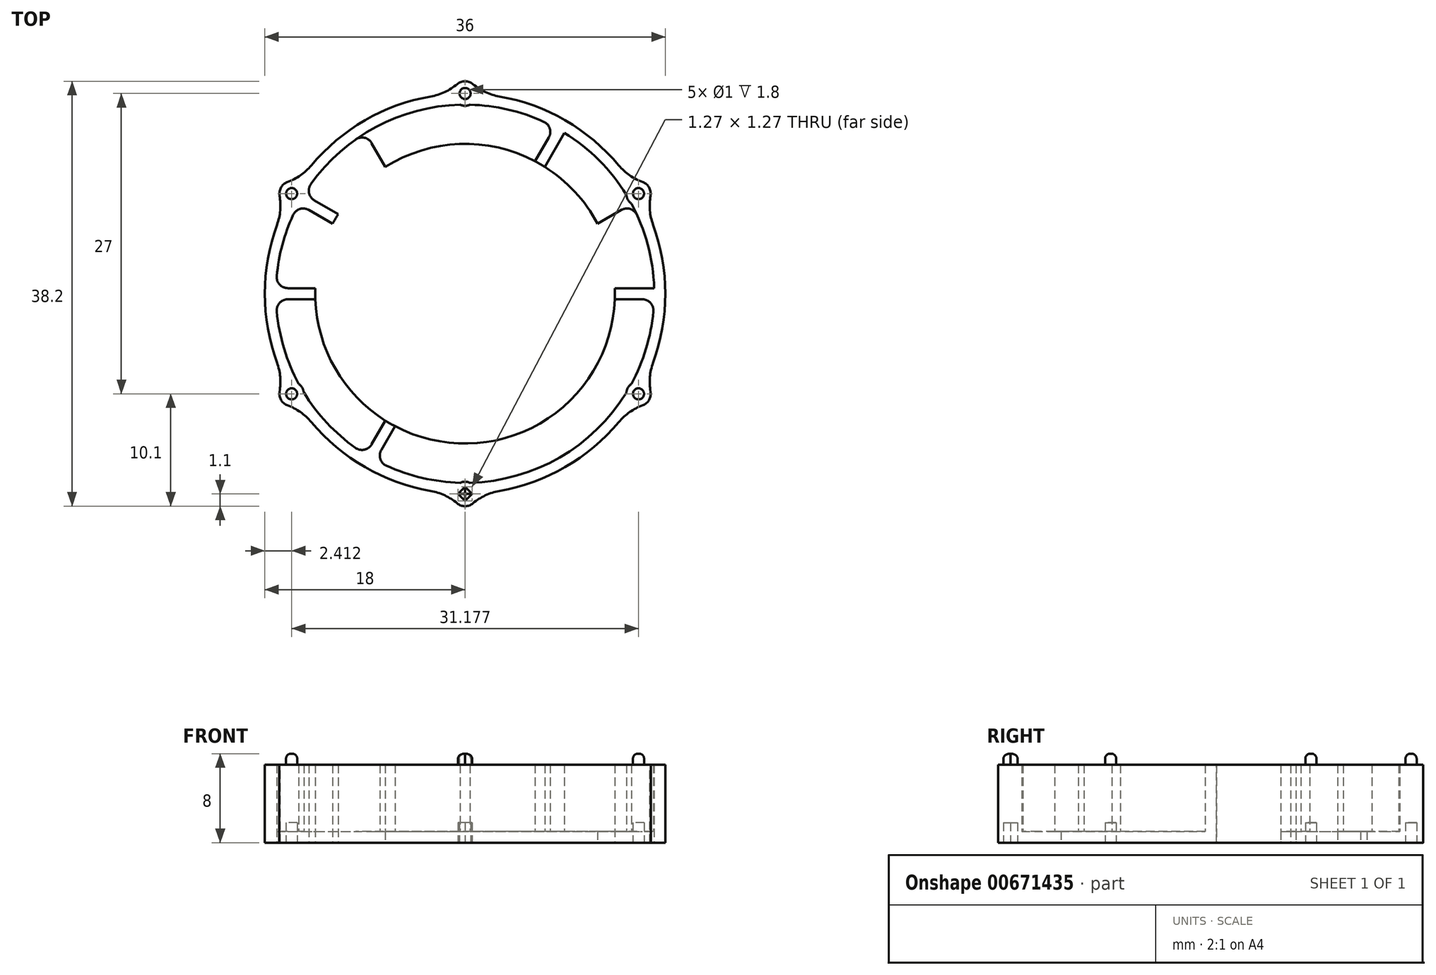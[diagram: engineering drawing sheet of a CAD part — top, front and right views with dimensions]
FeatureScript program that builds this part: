
annotation { "Feature Type Name" : "Feature", "Feature Type Description" : "" }
export const myFeature = defineFeature(function(context is Context, id is Id, definition is map)
    precondition{}
    {
        {
            var Q0;
            Q0=qCreatedBy(makeId("Top.planeOp"),FACE);
            var sketch = newSketch(context, id + "F0", { "sketchPlane" : qUnion([Q0])});
            skCircle(sketch, "E0", {"center": v(0, 0) * mm, "radius": 18 * mm});
            skCircle(sketch, "E1.0", {"center": v(0, 0) * mm, "radius": 17 * mm});
            skLineSegment(sketch, "E2.bottom", {"start": v(8.56, 15.83) * mm, "end": v(9.43, 15.33) * mm});
            skLineSegment(sketch, "E2.top", {"start": v(-9.43, -15.33) * mm, "end": v(-8.56, -15.83) * mm});
            skLineSegment(sketch, "E2.left", {"start": v(8.56, 15.83) * mm, "end": v(-9.43, -15.33) * mm});
            skLineSegment(sketch, "E2.right", {"start": v(9.43, 15.33) * mm, "end": v(-8.56, -15.83) * mm});
            skLineSegment(sketch, "E3.bottom", {"start": v(15.33, 9.43) * mm, "end": v(15.83, 8.56) * mm});
            skLineSegment(sketch, "E3.top", {"start": v(-15.83, -8.56) * mm, "end": v(-15.33, -9.43) * mm});
            skLineSegment(sketch, "E3.left", {"start": v(15.33, 9.43) * mm, "end": v(-15.83, -8.56) * mm});
            skLineSegment(sketch, "E3.right", {"start": v(15.83, 8.56) * mm, "end": v(-15.33, -9.43) * mm});
            skLineSegment(sketch, "E4", {"start": v(-38.35, 0) * mm, "end": v(39.17, 0) * mm, "construction": true});
            skLineSegment(sketch, "E5", {"start": v(0, 42.5) * mm, "end": v(0, -42.47) * mm, "construction": true});
            skLineSegment(sketch, "E6.bottom", {"start": v(-18, 0.5) * mm, "end": v(18, 0.5) * mm});
            skLineSegment(sketch, "E6.top", {"start": v(-18, -0.5) * mm, "end": v(18, -0.5) * mm});
            skLineSegment(sketch, "E6.left", {"start": v(-18, 0.5) * mm, "end": v(-18, -0.5) * mm});
            skLineSegment(sketch, "E6.right", {"start": v(18, 0.5) * mm, "end": v(18, -0.5) * mm});
            skLineSegment(sketch, "E7.bottom", {"start": v(-15.33, 9.43) * mm, "end": v(15.83, -8.56) * mm});
            skLineSegment(sketch, "E7.top", {"start": v(-15.83, 8.56) * mm, "end": v(15.33, -9.43) * mm});
            skLineSegment(sketch, "E7.left", {"start": v(-15.33, 9.43) * mm, "end": v(-15.83, 8.56) * mm});
            skLineSegment(sketch, "E7.right", {"start": v(15.83, -8.56) * mm, "end": v(15.33, -9.43) * mm});
            skLineSegment(sketch, "E8.bottom", {"start": v(-0.5, 18) * mm, "end": v(0.5, 18) * mm});
            skLineSegment(sketch, "E8.top", {"start": v(-0.5, -18) * mm, "end": v(0.5, -18) * mm});
            skLineSegment(sketch, "E8.left", {"start": v(-0.5, 18) * mm, "end": v(-0.5, -18) * mm});
            skLineSegment(sketch, "E8.right", {"start": v(0.5, 18) * mm, "end": v(0.5, -18) * mm});
            skLineSegment(sketch, "E9.bottom", {"start": v(-9.43, 15.33) * mm, "end": v(-8.56, 15.83) * mm});
            skLineSegment(sketch, "E9.top", {"start": v(8.56, -15.83) * mm, "end": v(9.43, -15.33) * mm});
            skLineSegment(sketch, "E9.left", {"start": v(-9.43, 15.33) * mm, "end": v(8.56, -15.83) * mm});
            skLineSegment(sketch, "E9.right", {"start": v(-8.56, 15.83) * mm, "end": v(9.43, -15.33) * mm});
            skCircle(sketch, "E10", {"center": v(0, 0) * mm, "radius": 13.47 * mm});
            skSolve(sketch);
        }
        {
            var Q0;
            Q0=qCreatedBy(makeId("Top.planeOp"),FACE);
            var sketch = newSketch(context, id + "F1", { "sketchPlane" : qUnion([Q0])});
            skCircle(sketch, "E11", {"center": v(0, 0) * mm, "radius": 18 * mm});
            skCircle(sketch, "E12", {"center": v(0, 0) * mm, "radius": 17 * mm});
            skSolve(sketch);
        }
        {
            var Q0;
            Q0=makeQuery(id+"F1.imprint","IMPRINT",FACE,{"disambiguationData":[TD([[makeQuery(id+"F1.imprint","IMPRINT",EDGE,{"derivedFrom":sQuery(id+"F1.wireOp",EDGE,"E11")}),1.0]])]});
            extrude(context, id + "F2", {"entities" : qUnion([Q0]), "depth" : 7 * mm, "offsetDistance" : 25 * mm});
        }
        {
            var Q0;
            {var subQ0=sQuery(id+"F0.wireOp",EDGE,"E7.bottom");var subQ1=sQuery(id+"F0.wireOp",EDGE,"E1.0");var subQ2=makeQuery(id+"F0.imprint","INTERSECT",VERTEX,{"disambiguationData":[OD(0.0)],"derivedFrom":[subQ1,subQ0]});Q0=makeQuery(id+"F0.imprint","IMPRINT",FACE,{"disambiguationData":[TD([[makeQuery(id+"F0.imprint","IMPRINT",EDGE,{"disambiguationData":[TD([[subQ2,-1.0]])],"derivedFrom":subQ1}),1.0]])]});}
            var Q1;
            {var subQ0=sQuery(id+"F0.wireOp",EDGE,"E2.right");var subQ1=sQuery(id+"F0.wireOp",EDGE,"E1.0");var subQ2=makeQuery(id+"F0.imprint","INTERSECT",VERTEX,{"disambiguationData":[OD(0.0)],"derivedFrom":[subQ1,subQ0]});Q1=makeQuery(id+"F0.imprint","IMPRINT",FACE,{"disambiguationData":[TD([[makeQuery(id+"F0.imprint","IMPRINT",EDGE,{"disambiguationData":[TD([[subQ2,-1.0]])],"derivedFrom":subQ1}),1.0]])]});}
            var Q2;
            {var subQ0=sQuery(id+"F0.wireOp",EDGE,"E6.bottom");var subQ1=sQuery(id+"F0.wireOp",EDGE,"E1.0");var subQ2=makeQuery(id+"F0.imprint","INTERSECT",VERTEX,{"disambiguationData":[OD(0.0)],"derivedFrom":[subQ1,subQ0]});Q2=makeQuery(id+"F0.imprint","IMPRINT",FACE,{"disambiguationData":[TD([[makeQuery(id+"F0.imprint","IMPRINT",EDGE,{"disambiguationData":[TD([[subQ2,1.0]])],"derivedFrom":subQ1}),1.0]])]});}
            var Q3;
            {var subQ0=sQuery(id+"F0.wireOp",EDGE,"E2.left");var subQ1=sQuery(id+"F0.wireOp",EDGE,"E1.0");var subQ2=makeQuery(id+"F0.imprint","INTERSECT",VERTEX,{"disambiguationData":[OD(1.0)],"derivedFrom":[subQ1,subQ0]});Q3=makeQuery(id+"F0.imprint","IMPRINT",FACE,{"disambiguationData":[TD([[makeQuery(id+"F0.imprint","IMPRINT",EDGE,{"disambiguationData":[TD([[subQ2,-1.0]])],"derivedFrom":subQ1}),1.0]])]});}
            var Q4;
            {var subQ0=sQuery(id+"F0.wireOp",EDGE,"E6.bottom");var subQ1=sQuery(id+"F0.wireOp",EDGE,"E1.0");var subQ2=makeQuery(id+"F0.imprint","INTERSECT",VERTEX,{"disambiguationData":[OD(1.0)],"derivedFrom":[subQ1,subQ0]});Q4=makeQuery(id+"F0.imprint","IMPRINT",FACE,{"disambiguationData":[TD([[makeQuery(id+"F0.imprint","IMPRINT",EDGE,{"disambiguationData":[TD([[subQ2,-1.0]])],"derivedFrom":subQ1}),1.0]])]});}
            extrude(context, id + "F3", {"entities" : qUnion([Q0, Q1, Q2, Q3, Q4]), "operationType" : NewBodyOperationType.ADD, "depth" : 7 * mm, "offsetDistance" : 25 * mm});
        }
        {
            var Q0;
            Q0=makeQuery(id+"F1.imprint","IMPRINT",FACE,{"disambiguationData":[TD([[makeQuery(id+"F1.imprint","IMPRINT",EDGE,{"derivedFrom":sQuery(id+"F1.wireOp",EDGE,"E11")}),1.0]])]});
            var Q1;
            Q1=makeQuery(id+"F1.imprint","IMPRINT",FACE,{"disambiguationData":[TD([[makeQuery(id+"F1.imprint","IMPRINT",EDGE,{"derivedFrom":sQuery(id+"F1.wireOp",EDGE,"E12")}),1.0]])]});
            extrude(context, id + "F4", {"entities" : qUnion([Q0, Q1]), "operationType" : NewBodyOperationType.ADD, "depth" : 1 * mm, "offsetDistance" : 25 * mm});
        }
        {
            var Q0;
            Q0=qCreatedBy(makeId("Top.planeOp"),FACE);
            var sketch = newSketch(context, id + "F5", { "sketchPlane" : qUnion([Q0])});
            skCircle(sketch, "E13", {"center": v(0, 0) * mm, "radius": 18 * mm});
            skLineSegment(sketch, "E14", {"start": v(0, 18) * mm, "end": v(0, -18) * mm, "construction": true});
            skLineSegment(sketch, "E15", {"start": v(15.59, 9) * mm, "end": v(0, 0) * mm, "construction": true});
            skLineSegment(sketch, "E16", {"start": v(9, 15.59) * mm, "end": v(0, 0) * mm, "construction": true});
            skLineSegment(sketch, "E17", {"start": v(0, 0) * mm, "end": v(18, 0) * mm, "construction": true});
            skLineSegment(sketch, "E18", {"start": v(0, 0) * mm, "end": v(15.59, -9) * mm, "construction": true});
            skLineSegment(sketch, "E19", {"start": v(0, 0) * mm, "end": v(9, -15.59) * mm, "construction": true});
            skLineSegment(sketch, "E20", {"start": v(0, 0) * mm, "end": v(-9, 15.59) * mm, "construction": true});
            skLineSegment(sketch, "E21", {"start": v(0, 0) * mm, "end": v(-15.59, 9) * mm, "construction": true});
            skLineSegment(sketch, "E22", {"start": v(0, 0) * mm, "end": v(-18, 0) * mm, "construction": true});
            skLineSegment(sketch, "E23", {"start": v(0, 0) * mm, "end": v(-15.59, -9) * mm, "construction": true});
            skLineSegment(sketch, "E24", {"start": v(0, 0) * mm, "end": v(-9, -15.59) * mm, "construction": true});
            skCircle(sketch, "E25", {"center": v(0, 18) * mm, "radius": 1.1 * mm});
            skCircle(sketch, "E26", {"center": v(15.59, 9) * mm, "radius": 1.1 * mm});
            skCircle(sketch, "E27", {"center": v(15.59, -9) * mm, "radius": 1.1 * mm});
            skCircle(sketch, "E28", {"center": v(0, -18) * mm, "radius": 1.1 * mm});
            skCircle(sketch, "E29", {"center": v(-15.59, -9) * mm, "radius": 1.1 * mm});
            skCircle(sketch, "E30", {"center": v(-15.59, 9) * mm, "radius": 1.1 * mm});
            skCircle(sketch, "E31", {"center": v(-15.59, 9) * mm, "radius": 0.5 * mm});
            skCircle(sketch, "E32", {"center": v(0, 18) * mm, "radius": 0.5 * mm});
            skCircle(sketch, "E33", {"center": v(15.59, 9) * mm, "radius": 0.5 * mm});
            skCircle(sketch, "E34", {"center": v(15.59, -9) * mm, "radius": 0.5 * mm});
            skCircle(sketch, "E35", {"center": v(-15.59, -9) * mm, "radius": 0.5 * mm});
            skLineSegment(sketch, "E36.bottom", {"start": v(0.64, -18) * mm, "end": v(0, -18.64) * mm});
            skLineSegment(sketch, "E36.top", {"start": v(0, -17.36) * mm, "end": v(-0.64, -18) * mm});
            skLineSegment(sketch, "E36.left", {"start": v(0.64, -18) * mm, "end": v(0, -17.36) * mm});
            skLineSegment(sketch, "E36.right", {"start": v(0, -18.64) * mm, "end": v(-0.64, -18) * mm});
            skSolve(sketch);
        }
        {
            var Q0;
            {var subQ0=sQuery(id+"F5.wireOp",EDGE,"E30");var subQ1=sQuery(id+"F5.wireOp",EDGE,"E13");var subQ2=makeQuery(id+"F5.imprint","INTERSECT",VERTEX,{"disambiguationData":[OD(0.0)],"derivedFrom":[subQ1,subQ0]});Q0=makeQuery(id+"F5.imprint","IMPRINT",FACE,{"disambiguationData":[TD([[makeQuery(id+"F5.imprint","IMPRINT",EDGE,{"disambiguationData":[TD([[subQ2,-1.0]])],"derivedFrom":subQ1}),1.0]])]});}
            var Q1;
            {var subQ0=sQuery(id+"F5.wireOp",EDGE,"E30");var subQ1=sQuery(id+"F5.wireOp",EDGE,"E13");var subQ2=makeQuery(id+"F5.imprint","INTERSECT",VERTEX,{"disambiguationData":[OD(0.0)],"derivedFrom":[subQ1,subQ0]});Q1=makeQuery(id+"F5.imprint","IMPRINT",FACE,{"disambiguationData":[TD([[makeQuery(id+"F5.imprint","IMPRINT",EDGE,{"disambiguationData":[TD([[subQ2,-1.0]])],"derivedFrom":subQ1}),-1.0]])]});}
            var Q2;
            {var subQ0=sQuery(id+"F5.wireOp",EDGE,"E25");var subQ1=sQuery(id+"F5.wireOp",EDGE,"E13");var subQ2=makeQuery(id+"F5.imprint","INTERSECT",VERTEX,{"disambiguationData":[OD(0.0)],"derivedFrom":[subQ1,subQ0]});Q2=makeQuery(id+"F5.imprint","IMPRINT",FACE,{"disambiguationData":[TD([[makeQuery(id+"F5.imprint","IMPRINT",EDGE,{"disambiguationData":[TD([[subQ2,-1.0]])],"derivedFrom":subQ1}),1.0]])]});}
            var Q3;
            {var subQ0=sQuery(id+"F5.wireOp",EDGE,"E25");var subQ1=sQuery(id+"F5.wireOp",EDGE,"E13");var subQ2=makeQuery(id+"F5.imprint","INTERSECT",VERTEX,{"disambiguationData":[OD(0.0)],"derivedFrom":[subQ1,subQ0]});Q3=makeQuery(id+"F5.imprint","IMPRINT",FACE,{"disambiguationData":[TD([[makeQuery(id+"F5.imprint","IMPRINT",EDGE,{"disambiguationData":[TD([[subQ2,-1.0]])],"derivedFrom":subQ1}),-1.0]])]});}
            var Q4;
            {var subQ0=sQuery(id+"F5.wireOp",EDGE,"E26");var subQ1=sQuery(id+"F5.wireOp",EDGE,"E13");var subQ2=makeQuery(id+"F5.imprint","INTERSECT",VERTEX,{"disambiguationData":[OD(0.0)],"derivedFrom":[subQ1,subQ0]});Q4=makeQuery(id+"F5.imprint","IMPRINT",FACE,{"disambiguationData":[TD([[makeQuery(id+"F5.imprint","IMPRINT",EDGE,{"disambiguationData":[TD([[subQ2,-1.0]])],"derivedFrom":subQ1}),-1.0]])]});}
            var Q5;
            {var subQ0=sQuery(id+"F5.wireOp",EDGE,"E26");var subQ1=sQuery(id+"F5.wireOp",EDGE,"E13");var subQ2=makeQuery(id+"F5.imprint","INTERSECT",VERTEX,{"disambiguationData":[OD(0.0)],"derivedFrom":[subQ1,subQ0]});Q5=makeQuery(id+"F5.imprint","IMPRINT",FACE,{"disambiguationData":[TD([[makeQuery(id+"F5.imprint","IMPRINT",EDGE,{"disambiguationData":[TD([[subQ2,-1.0]])],"derivedFrom":subQ1}),1.0]])]});}
            var Q6;
            {var subQ0=sQuery(id+"F5.wireOp",EDGE,"E29");var subQ1=sQuery(id+"F5.wireOp",EDGE,"E13");var subQ2=makeQuery(id+"F5.imprint","INTERSECT",VERTEX,{"disambiguationData":[OD(0.0)],"derivedFrom":[subQ1,subQ0]});Q6=makeQuery(id+"F5.imprint","IMPRINT",FACE,{"disambiguationData":[TD([[makeQuery(id+"F5.imprint","IMPRINT",EDGE,{"disambiguationData":[TD([[subQ2,-1.0]])],"derivedFrom":subQ1}),1.0]])]});}
            var Q7;
            {var subQ0=sQuery(id+"F5.wireOp",EDGE,"E29");var subQ1=sQuery(id+"F5.wireOp",EDGE,"E13");var subQ2=makeQuery(id+"F5.imprint","INTERSECT",VERTEX,{"disambiguationData":[OD(0.0)],"derivedFrom":[subQ1,subQ0]});Q7=makeQuery(id+"F5.imprint","IMPRINT",FACE,{"disambiguationData":[TD([[makeQuery(id+"F5.imprint","IMPRINT",EDGE,{"disambiguationData":[TD([[subQ2,-1.0]])],"derivedFrom":subQ1}),-1.0]])]});}
            var Q8;
            {var subQ3=sQuery(id+"F5.wireOp",EDGE,"E13");var subQ5=sQuery(id+"F5.wireOp",EDGE,"E28");var subQ6=makeQuery(id+"F5.imprint","INTERSECT",VERTEX,{"disambiguationData":[OD(0.0)],"derivedFrom":[subQ3,subQ5]});Q8=makeQuery(id+"F5.imprint","IMPRINT",FACE,{"disambiguationData":[TD([[makeQuery(id+"F5.imprint","IMPRINT",EDGE,{"disambiguationData":[TD([[subQ6,-1.0]])],"derivedFrom":subQ3}),1.0]])]});}
            var Q9;
            {var subQ6=sQuery(id+"F5.wireOp",EDGE,"E36.bottom");Q9=makeQuery(id+"F5.imprint","IMPRINT",FACE,{"disambiguationData":[TD([[makeQuery(id+"F5.imprint","IMPRINT",EDGE,{"derivedFrom":subQ6}),1.0]])]});}
            var Q10;
            {var subQ0=sQuery(id+"F5.wireOp",EDGE,"E27");var subQ1=sQuery(id+"F5.wireOp",EDGE,"E13");var subQ2=makeQuery(id+"F5.imprint","INTERSECT",VERTEX,{"disambiguationData":[OD(0.0)],"derivedFrom":[subQ1,subQ0]});Q10=makeQuery(id+"F5.imprint","IMPRINT",FACE,{"disambiguationData":[TD([[makeQuery(id+"F5.imprint","IMPRINT",EDGE,{"disambiguationData":[TD([[subQ2,-1.0]])],"derivedFrom":subQ1}),-1.0]])]});}
            var Q11;
            {var subQ0=sQuery(id+"F5.wireOp",EDGE,"E27");var subQ1=sQuery(id+"F5.wireOp",EDGE,"E13");var subQ2=makeQuery(id+"F5.imprint","INTERSECT",VERTEX,{"disambiguationData":[OD(0.0)],"derivedFrom":[subQ1,subQ0]});Q11=makeQuery(id+"F5.imprint","IMPRINT",FACE,{"disambiguationData":[TD([[makeQuery(id+"F5.imprint","IMPRINT",EDGE,{"disambiguationData":[TD([[subQ2,-1.0]])],"derivedFrom":subQ1}),1.0]])]});}
            var Q12;
            {var subQ0=sQuery(id+"F5.wireOp",EDGE,"E31");var subQ1=sQuery(id+"F5.wireOp",EDGE,"E13");var subQ2=makeQuery(id+"F5.imprint","INTERSECT",VERTEX,{"disambiguationData":[OD(0.0)],"derivedFrom":[subQ1,subQ0]});Q12=makeQuery(id+"F5.imprint","IMPRINT",FACE,{"disambiguationData":[TD([[makeQuery(id+"F5.imprint","IMPRINT",EDGE,{"disambiguationData":[TD([[subQ2,-1.0]])],"derivedFrom":subQ1}),1.0]])]});}
            var Q13;
            {var subQ0=sQuery(id+"F5.wireOp",EDGE,"E31");var subQ1=sQuery(id+"F5.wireOp",EDGE,"E13");var subQ2=makeQuery(id+"F5.imprint","INTERSECT",VERTEX,{"disambiguationData":[OD(0.0)],"derivedFrom":[subQ1,subQ0]});Q13=makeQuery(id+"F5.imprint","IMPRINT",FACE,{"disambiguationData":[TD([[makeQuery(id+"F5.imprint","IMPRINT",EDGE,{"disambiguationData":[TD([[subQ2,-1.0]])],"derivedFrom":subQ1}),-1.0]])]});}
            var Q14;
            {var subQ0=sQuery(id+"F5.wireOp",EDGE,"E32");var subQ1=sQuery(id+"F5.wireOp",EDGE,"E13");var subQ2=makeQuery(id+"F5.imprint","INTERSECT",VERTEX,{"disambiguationData":[OD(0.0)],"derivedFrom":[subQ1,subQ0]});Q14=makeQuery(id+"F5.imprint","IMPRINT",FACE,{"disambiguationData":[TD([[makeQuery(id+"F5.imprint","IMPRINT",EDGE,{"disambiguationData":[TD([[subQ2,-1.0]])],"derivedFrom":subQ1}),-1.0]])]});}
            var Q15;
            {var subQ0=sQuery(id+"F5.wireOp",EDGE,"E32");var subQ1=sQuery(id+"F5.wireOp",EDGE,"E13");var subQ2=makeQuery(id+"F5.imprint","INTERSECT",VERTEX,{"disambiguationData":[OD(0.0)],"derivedFrom":[subQ1,subQ0]});Q15=makeQuery(id+"F5.imprint","IMPRINT",FACE,{"disambiguationData":[TD([[makeQuery(id+"F5.imprint","IMPRINT",EDGE,{"disambiguationData":[TD([[subQ2,-1.0]])],"derivedFrom":subQ1}),1.0]])]});}
            var Q16;
            {var subQ0=sQuery(id+"F5.wireOp",EDGE,"E33");var subQ1=sQuery(id+"F5.wireOp",EDGE,"E13");var subQ2=makeQuery(id+"F5.imprint","INTERSECT",VERTEX,{"disambiguationData":[OD(0.0)],"derivedFrom":[subQ1,subQ0]});Q16=makeQuery(id+"F5.imprint","IMPRINT",FACE,{"disambiguationData":[TD([[makeQuery(id+"F5.imprint","IMPRINT",EDGE,{"disambiguationData":[TD([[subQ2,-1.0]])],"derivedFrom":subQ1}),-1.0]])]});}
            var Q17;
            {var subQ0=sQuery(id+"F5.wireOp",EDGE,"E33");var subQ1=sQuery(id+"F5.wireOp",EDGE,"E13");var subQ2=makeQuery(id+"F5.imprint","INTERSECT",VERTEX,{"disambiguationData":[OD(0.0)],"derivedFrom":[subQ1,subQ0]});Q17=makeQuery(id+"F5.imprint","IMPRINT",FACE,{"disambiguationData":[TD([[makeQuery(id+"F5.imprint","IMPRINT",EDGE,{"disambiguationData":[TD([[subQ2,-1.0]])],"derivedFrom":subQ1}),1.0]])]});}
            var Q18;
            {var subQ0=sQuery(id+"F5.wireOp",EDGE,"E34");var subQ1=sQuery(id+"F5.wireOp",EDGE,"E13");var subQ2=makeQuery(id+"F5.imprint","INTERSECT",VERTEX,{"disambiguationData":[OD(0.0)],"derivedFrom":[subQ1,subQ0]});Q18=makeQuery(id+"F5.imprint","IMPRINT",FACE,{"disambiguationData":[TD([[makeQuery(id+"F5.imprint","IMPRINT",EDGE,{"disambiguationData":[TD([[subQ2,-1.0]])],"derivedFrom":subQ1}),-1.0]])]});}
            var Q19;
            {var subQ0=sQuery(id+"F5.wireOp",EDGE,"E34");var subQ1=sQuery(id+"F5.wireOp",EDGE,"E13");var subQ2=makeQuery(id+"F5.imprint","INTERSECT",VERTEX,{"disambiguationData":[OD(0.0)],"derivedFrom":[subQ1,subQ0]});Q19=makeQuery(id+"F5.imprint","IMPRINT",FACE,{"disambiguationData":[TD([[makeQuery(id+"F5.imprint","IMPRINT",EDGE,{"disambiguationData":[TD([[subQ2,-1.0]])],"derivedFrom":subQ1}),1.0]])]});}
            var Q20;
            {var subQ1=sQuery(id+"F5.wireOp",EDGE,"E36.bottom");Q20=makeQuery(id+"F5.imprint","IMPRINT",FACE,{"disambiguationData":[TD([[makeQuery(id+"F5.imprint","IMPRINT",EDGE,{"derivedFrom":subQ1}),-1.0]])]});}
            var Q21;
            {var subQ0=sQuery(id+"F5.wireOp",EDGE,"E35");var subQ1=sQuery(id+"F5.wireOp",EDGE,"E13");var subQ2=makeQuery(id+"F5.imprint","INTERSECT",VERTEX,{"disambiguationData":[OD(0.0)],"derivedFrom":[subQ1,subQ0]});Q21=makeQuery(id+"F5.imprint","IMPRINT",FACE,{"disambiguationData":[TD([[makeQuery(id+"F5.imprint","IMPRINT",EDGE,{"disambiguationData":[TD([[subQ2,-1.0]])],"derivedFrom":subQ1}),-1.0]])]});}
            var Q22;
            {var subQ0=sQuery(id+"F5.wireOp",EDGE,"E35");var subQ1=sQuery(id+"F5.wireOp",EDGE,"E13");var subQ2=makeQuery(id+"F5.imprint","INTERSECT",VERTEX,{"disambiguationData":[OD(0.0)],"derivedFrom":[subQ1,subQ0]});Q22=makeQuery(id+"F5.imprint","IMPRINT",FACE,{"disambiguationData":[TD([[makeQuery(id+"F5.imprint","IMPRINT",EDGE,{"disambiguationData":[TD([[subQ2,-1.0]])],"derivedFrom":subQ1}),1.0]])]});}
            var Q23;
            {var subQ0=sQuery(id+"F5.wireOp",EDGE,"E36.top");var subQ1=sQuery(id+"F5.wireOp",EDGE,"E13");var subQ2=makeQuery(id+"F5.imprint","INTERSECT",VERTEX,{"derivedFrom":[subQ1,subQ0]});Q23=makeQuery(id+"F5.imprint","IMPRINT",FACE,{"disambiguationData":[TD([[makeQuery(id+"F5.imprint","IMPRINT",EDGE,{"disambiguationData":[TD([[subQ2,-1.0]])],"derivedFrom":subQ1}),1.0]])]});}
            extrude(context, id + "F6", {"entities" : qUnion([Q0, Q1, Q2, Q3, Q4, Q5, Q6, Q7, Q8, Q9, Q10, Q11, Q12, Q13, Q14, Q15, Q16, Q17, Q18, Q19, Q20, Q21, Q22, Q23]), "operationType" : NewBodyOperationType.ADD, "depth" : 7 * mm, "offsetDistance" : 25 * mm});
        }
        {
            var Q0;
            {var subQ0=sQuery(id+"F0.wireOp",EDGE,"E8.right");var subQ1=sQuery(id+"F0.wireOp",EDGE,"E1.0");Q0=makeQuery(id+"F3.opExtrude","SWEPT_EDGE",EDGE,{"disambiguationData":[OSD([subQ1,subQ0]),TDD([makeQuery(id+"F0.imprint","INTERSECT",VERTEX,{"disambiguationData":[OD(1.0)],"derivedFrom":[subQ1,subQ0]})])]});}
            var Q1;
            {var subQ0=sQuery(id+"F0.wireOp",EDGE,"E2.left");var subQ1=sQuery(id+"F0.wireOp",EDGE,"E1.0");Q1=makeQuery(id+"F3.opExtrude","SWEPT_EDGE",EDGE,{"disambiguationData":[OSD([subQ1,subQ0]),TDD([makeQuery(id+"F0.imprint","INTERSECT",VERTEX,{"disambiguationData":[OD(1.0)],"derivedFrom":[subQ1,subQ0]})])]});}
            var Q2;
            {var subQ0=sQuery(id+"F0.wireOp",EDGE,"E3.left");var subQ1=sQuery(id+"F0.wireOp",EDGE,"E1.0");Q2=makeQuery(id+"F3.opExtrude","SWEPT_EDGE",EDGE,{"disambiguationData":[OSD([subQ1,subQ0]),TDD([makeQuery(id+"F0.imprint","INTERSECT",VERTEX,{"disambiguationData":[OD(1.0)],"derivedFrom":[subQ1,subQ0]})])]});}
            var Q3;
            {var subQ0=sQuery(id+"F0.wireOp",EDGE,"E6.bottom");var subQ1=sQuery(id+"F0.wireOp",EDGE,"E1.0");Q3=makeQuery(id+"F3.opExtrude","SWEPT_EDGE",EDGE,{"disambiguationData":[OSD([subQ1,subQ0]),TDD([makeQuery(id+"F0.imprint","INTERSECT",VERTEX,{"disambiguationData":[OD(1.0)],"derivedFrom":[subQ1,subQ0]})])]});}
            var Q4;
            {var subQ0=sQuery(id+"F0.wireOp",EDGE,"E9.right");var subQ1=sQuery(id+"F0.wireOp",EDGE,"E1.0");Q4=makeQuery(id+"F3.opExtrude","SWEPT_EDGE",EDGE,{"disambiguationData":[OSD([subQ1,subQ0]),TDD([makeQuery(id+"F0.imprint","INTERSECT",VERTEX,{"disambiguationData":[OD(1.0)],"derivedFrom":[subQ1,subQ0]})])]});}
            var Q5;
            {var subQ0=sQuery(id+"F0.wireOp",EDGE,"E7.bottom");var subQ1=sQuery(id+"F0.wireOp",EDGE,"E1.0");Q5=makeQuery(id+"F3.opExtrude","SWEPT_EDGE",EDGE,{"disambiguationData":[OSD([subQ1,subQ0]),TDD([makeQuery(id+"F0.imprint","INTERSECT",VERTEX,{"disambiguationData":[OD(1.0)],"derivedFrom":[subQ1,subQ0]})])]});}
            var Q6;
            {var subQ0=sQuery(id+"F0.wireOp",EDGE,"E8.left");var subQ1=sQuery(id+"F0.wireOp",EDGE,"E1.0");Q6=makeQuery(id+"F3.opExtrude","SWEPT_EDGE",EDGE,{"disambiguationData":[OSD([subQ1,subQ0]),TDD([makeQuery(id+"F0.imprint","INTERSECT",VERTEX,{"disambiguationData":[OD(0.0)],"derivedFrom":[subQ1,subQ0]})])]});}
            var Q7;
            {var subQ0=sQuery(id+"F0.wireOp",EDGE,"E2.left");var subQ1=sQuery(id+"F0.wireOp",EDGE,"E1.0");Q7=makeQuery(id+"F3.opExtrude","SWEPT_EDGE",EDGE,{"disambiguationData":[OSD([subQ1,subQ0]),TDD([makeQuery(id+"F0.imprint","INTERSECT",VERTEX,{"disambiguationData":[OD(0.0)],"derivedFrom":[subQ1,subQ0]})])]});}
            var Q8;
            {var subQ0=sQuery(id+"F0.wireOp",EDGE,"E3.left");var subQ1=sQuery(id+"F0.wireOp",EDGE,"E1.0");Q8=makeQuery(id+"F3.opExtrude","SWEPT_EDGE",EDGE,{"disambiguationData":[OSD([subQ1,subQ0]),TDD([makeQuery(id+"F0.imprint","INTERSECT",VERTEX,{"disambiguationData":[OD(0.0)],"derivedFrom":[subQ1,subQ0]})])]});}
            var Q9;
            {var subQ0=sQuery(id+"F0.wireOp",EDGE,"E6.top");var subQ1=sQuery(id+"F0.wireOp",EDGE,"E1.0");Q9=makeQuery(id+"F3.opExtrude","SWEPT_EDGE",EDGE,{"disambiguationData":[OSD([subQ1,subQ0]),TDD([makeQuery(id+"F0.imprint","INTERSECT",VERTEX,{"disambiguationData":[OD(1.0)],"derivedFrom":[subQ1,subQ0]})])]});}
            var Q10;
            {var subQ0=sQuery(id+"F0.wireOp",EDGE,"E7.top");var subQ1=sQuery(id+"F0.wireOp",EDGE,"E1.0");Q10=makeQuery(id+"F3.opExtrude","SWEPT_EDGE",EDGE,{"disambiguationData":[OSD([subQ1,subQ0]),TDD([makeQuery(id+"F0.imprint","INTERSECT",VERTEX,{"disambiguationData":[OD(0.0)],"derivedFrom":[subQ1,subQ0]})])]});}
            var Q11;
            {var subQ0=sQuery(id+"F0.wireOp",EDGE,"E6.top");var subQ1=sQuery(id+"F0.wireOp",EDGE,"E1.0");Q11=makeQuery(id+"F3.opExtrude","SWEPT_EDGE",EDGE,{"disambiguationData":[OSD([subQ1,subQ0]),TDD([makeQuery(id+"F0.imprint","INTERSECT",VERTEX,{"disambiguationData":[OD(0.0)],"derivedFrom":[subQ1,subQ0]})])]});}
            var Q12;
            {var subQ0=sQuery(id+"F0.wireOp",EDGE,"E9.left");var subQ1=sQuery(id+"F0.wireOp",EDGE,"E1.0");Q12=makeQuery(id+"F3.opExtrude","SWEPT_EDGE",EDGE,{"disambiguationData":[OSD([subQ1,subQ0]),TDD([makeQuery(id+"F0.imprint","INTERSECT",VERTEX,{"disambiguationData":[OD(0.0)],"derivedFrom":[subQ1,subQ0]})])]});}
            var Q13;
            {var subQ0=sQuery(id+"F0.wireOp",EDGE,"E8.right");var subQ1=sQuery(id+"F0.wireOp",EDGE,"E1.0");Q13=makeQuery(id+"F3.opExtrude","SWEPT_EDGE",EDGE,{"disambiguationData":[OSD([subQ1,subQ0]),TDD([makeQuery(id+"F0.imprint","INTERSECT",VERTEX,{"disambiguationData":[OD(0.0)],"derivedFrom":[subQ1,subQ0]})])]});}
            var Q14;
            {var subQ0=sQuery(id+"F0.wireOp",EDGE,"E7.bottom");var subQ1=sQuery(id+"F0.wireOp",EDGE,"E1.0");Q14=makeQuery(id+"F3.opExtrude","SWEPT_EDGE",EDGE,{"disambiguationData":[OSD([subQ1,subQ0]),TDD([makeQuery(id+"F0.imprint","INTERSECT",VERTEX,{"disambiguationData":[OD(0.0)],"derivedFrom":[subQ1,subQ0]})])]});}
            var Q15;
            {var subQ0=sQuery(id+"F0.wireOp",EDGE,"E9.right");var subQ1=sQuery(id+"F0.wireOp",EDGE,"E1.0");Q15=makeQuery(id+"F3.opExtrude","SWEPT_EDGE",EDGE,{"disambiguationData":[OSD([subQ1,subQ0]),TDD([makeQuery(id+"F0.imprint","INTERSECT",VERTEX,{"disambiguationData":[OD(0.0)],"derivedFrom":[subQ1,subQ0]})])]});}
            var Q16;
            {var subQ0=sQuery(id+"F0.wireOp",EDGE,"E3.right");var subQ1=sQuery(id+"F0.wireOp",EDGE,"E1.0");Q16=makeQuery(id+"F3.opExtrude","SWEPT_EDGE",EDGE,{"disambiguationData":[OSD([subQ1,subQ0]),TDD([makeQuery(id+"F0.imprint","INTERSECT",VERTEX,{"disambiguationData":[OD(1.0)],"derivedFrom":[subQ1,subQ0]})])]});}
            var Q17;
            {var subQ0=sQuery(id+"F0.wireOp",EDGE,"E2.right");var subQ1=sQuery(id+"F0.wireOp",EDGE,"E1.0");Q17=makeQuery(id+"F3.opExtrude","SWEPT_EDGE",EDGE,{"disambiguationData":[OSD([subQ1,subQ0]),TDD([makeQuery(id+"F0.imprint","INTERSECT",VERTEX,{"disambiguationData":[OD(1.0)],"derivedFrom":[subQ1,subQ0]})])]});}
            var Q18;
            {var subQ0=sQuery(id+"F0.wireOp",EDGE,"E3.right");var subQ1=sQuery(id+"F0.wireOp",EDGE,"E1.0");Q18=makeQuery(id+"F3.opExtrude","SWEPT_EDGE",EDGE,{"disambiguationData":[OSD([subQ1,subQ0]),TDD([makeQuery(id+"F0.imprint","INTERSECT",VERTEX,{"disambiguationData":[OD(0.0)],"derivedFrom":[subQ1,subQ0]})])]});}
            var Q19;
            {var subQ0=sQuery(id+"F0.wireOp",EDGE,"E2.right");var subQ1=sQuery(id+"F0.wireOp",EDGE,"E1.0");Q19=makeQuery(id+"F3.opExtrude","SWEPT_EDGE",EDGE,{"disambiguationData":[OSD([subQ1,subQ0]),TDD([makeQuery(id+"F0.imprint","INTERSECT",VERTEX,{"disambiguationData":[OD(0.0)],"derivedFrom":[subQ1,subQ0]})])]});}
            var Q20;
            {var subQ0=sQuery(id+"F0.wireOp",EDGE,"E8.left");var subQ1=sQuery(id+"F0.wireOp",EDGE,"E1.0");Q20=makeQuery(id+"F3.opExtrude","SWEPT_EDGE",EDGE,{"disambiguationData":[OSD([subQ1,subQ0]),TDD([makeQuery(id+"F0.imprint","INTERSECT",VERTEX,{"disambiguationData":[OD(1.0)],"derivedFrom":[subQ1,subQ0]})])]});}
            var Q21;
            {var subQ0=sQuery(id+"F0.wireOp",EDGE,"E9.left");var subQ1=sQuery(id+"F0.wireOp",EDGE,"E1.0");Q21=makeQuery(id+"F3.opExtrude","SWEPT_EDGE",EDGE,{"disambiguationData":[OSD([subQ1,subQ0]),TDD([makeQuery(id+"F0.imprint","INTERSECT",VERTEX,{"disambiguationData":[OD(1.0)],"derivedFrom":[subQ1,subQ0]})])]});}
            var Q22;
            {var subQ0=sQuery(id+"F0.wireOp",EDGE,"E7.top");var subQ1=sQuery(id+"F0.wireOp",EDGE,"E1.0");Q22=makeQuery(id+"F3.opExtrude","SWEPT_EDGE",EDGE,{"disambiguationData":[OSD([subQ1,subQ0]),TDD([makeQuery(id+"F0.imprint","INTERSECT",VERTEX,{"disambiguationData":[OD(1.0)],"derivedFrom":[subQ1,subQ0]})])]});}
            var Q23;
            {var subQ0=sQuery(id+"F0.wireOp",EDGE,"E6.bottom");var subQ1=sQuery(id+"F0.wireOp",EDGE,"E1.0");Q23=makeQuery(id+"F3.opExtrude","SWEPT_EDGE",EDGE,{"disambiguationData":[OSD([subQ1,subQ0]),TDD([makeQuery(id+"F0.imprint","INTERSECT",VERTEX,{"disambiguationData":[OD(0.0)],"derivedFrom":[subQ1,subQ0]})])]});}
            fillet(context, id + "F7", {"entities" : qUnion([Q0, Q1, Q2, Q3, Q4, Q5, Q6, Q7, Q8, Q9, Q10, Q11, Q12, Q13, Q14, Q15, Q16, Q17, Q18, Q19, Q20, Q21, Q22, Q23]), "radius" : 1 * mm, "tangentPropagation" : true, "allowEdgeOverflow" : false});
        }
        {
            var Q0;
            Q0=makeQuery(id+"F6.boolean.opBoolean","INTERSECT",EDGE,{"disambiguationData":[OD(0.0)],"derivedFrom":[makeQuery(id+"F2.opExtrude","SWEPT_FACE",FACE,{"disambiguationData":[OSD([sQuery(id+"F1.wireOp",EDGE,"E11")])]}),makeQuery(id+"F6.opExtrude","SWEPT_FACE",FACE,{"disambiguationData":[OSD([sQuery(id+"F5.wireOp",EDGE,"E30")])]})]});
            var Q1;
            Q1=makeQuery(id+"F6.boolean.opBoolean","INTERSECT",EDGE,{"disambiguationData":[OD(1.0)],"derivedFrom":[makeQuery(id+"F2.opExtrude","SWEPT_FACE",FACE,{"disambiguationData":[OSD([sQuery(id+"F1.wireOp",EDGE,"E11")])]}),makeQuery(id+"F6.opExtrude","SWEPT_FACE",FACE,{"disambiguationData":[OSD([sQuery(id+"F5.wireOp",EDGE,"E30")])]})]});
            var Q2;
            Q2=makeQuery(id+"F6.boolean.opBoolean","INTERSECT",EDGE,{"disambiguationData":[OD(1.0)],"derivedFrom":[makeQuery(id+"F2.opExtrude","SWEPT_FACE",FACE,{"disambiguationData":[OSD([sQuery(id+"F1.wireOp",EDGE,"E11")])]}),makeQuery(id+"F6.opExtrude","SWEPT_FACE",FACE,{"disambiguationData":[OSD([sQuery(id+"F5.wireOp",EDGE,"E25")])]})]});
            var Q3;
            Q3=makeQuery(id+"F6.boolean.opBoolean","INTERSECT",EDGE,{"disambiguationData":[OD(1.0)],"derivedFrom":[makeQuery(id+"F2.opExtrude","SWEPT_FACE",FACE,{"disambiguationData":[OSD([sQuery(id+"F1.wireOp",EDGE,"E11")])]}),makeQuery(id+"F6.opExtrude","SWEPT_FACE",FACE,{"disambiguationData":[OSD([sQuery(id+"F5.wireOp",EDGE,"E29")])]})]});
            var Q4;
            Q4=makeQuery(id+"F6.boolean.opBoolean","INTERSECT",EDGE,{"disambiguationData":[OD(0.0)],"derivedFrom":[makeQuery(id+"F2.opExtrude","SWEPT_FACE",FACE,{"disambiguationData":[OSD([sQuery(id+"F1.wireOp",EDGE,"E11")])]}),makeQuery(id+"F6.opExtrude","SWEPT_FACE",FACE,{"disambiguationData":[OSD([sQuery(id+"F5.wireOp",EDGE,"E29")])]})]});
            var Q5;
            Q5=makeQuery(id+"F6.boolean.opBoolean","INTERSECT",EDGE,{"disambiguationData":[OD(1.0)],"derivedFrom":[makeQuery(id+"F2.opExtrude","SWEPT_FACE",FACE,{"disambiguationData":[OSD([sQuery(id+"F1.wireOp",EDGE,"E11")])]}),makeQuery(id+"F6.opExtrude","SWEPT_FACE",FACE,{"disambiguationData":[OSD([sQuery(id+"F5.wireOp",EDGE,"E28")])]})]});
            var Q6;
            Q6=makeQuery(id+"F6.boolean.opBoolean","INTERSECT",EDGE,{"disambiguationData":[OD(0.0)],"derivedFrom":[makeQuery(id+"F2.opExtrude","SWEPT_FACE",FACE,{"disambiguationData":[OSD([sQuery(id+"F1.wireOp",EDGE,"E11")])]}),makeQuery(id+"F6.opExtrude","SWEPT_FACE",FACE,{"disambiguationData":[OSD([sQuery(id+"F5.wireOp",EDGE,"E28")])]})]});
            var Q7;
            Q7=makeQuery(id+"F6.boolean.opBoolean","INTERSECT",EDGE,{"disambiguationData":[OD(1.0)],"derivedFrom":[makeQuery(id+"F2.opExtrude","SWEPT_FACE",FACE,{"disambiguationData":[OSD([sQuery(id+"F1.wireOp",EDGE,"E11")])]}),makeQuery(id+"F6.opExtrude","SWEPT_FACE",FACE,{"disambiguationData":[OSD([sQuery(id+"F5.wireOp",EDGE,"E27")])]})]});
            var Q8;
            Q8=makeQuery(id+"F6.boolean.opBoolean","INTERSECT",EDGE,{"disambiguationData":[OD(0.0)],"derivedFrom":[makeQuery(id+"F2.opExtrude","SWEPT_FACE",FACE,{"disambiguationData":[OSD([sQuery(id+"F1.wireOp",EDGE,"E11")])]}),makeQuery(id+"F6.opExtrude","SWEPT_FACE",FACE,{"disambiguationData":[OSD([sQuery(id+"F5.wireOp",EDGE,"E27")])]})]});
            var Q9;
            Q9=makeQuery(id+"F6.boolean.opBoolean","INTERSECT",EDGE,{"disambiguationData":[OD(1.0)],"derivedFrom":[makeQuery(id+"F2.opExtrude","SWEPT_FACE",FACE,{"disambiguationData":[OSD([sQuery(id+"F1.wireOp",EDGE,"E11")])]}),makeQuery(id+"F6.opExtrude","SWEPT_FACE",FACE,{"disambiguationData":[OSD([sQuery(id+"F5.wireOp",EDGE,"E26")])]})]});
            var Q10;
            Q10=makeQuery(id+"F6.boolean.opBoolean","INTERSECT",EDGE,{"disambiguationData":[OD(0.0)],"derivedFrom":[makeQuery(id+"F2.opExtrude","SWEPT_FACE",FACE,{"disambiguationData":[OSD([sQuery(id+"F1.wireOp",EDGE,"E11")])]}),makeQuery(id+"F6.opExtrude","SWEPT_FACE",FACE,{"disambiguationData":[OSD([sQuery(id+"F5.wireOp",EDGE,"E26")])]})]});
            var Q11;
            Q11=makeQuery(id+"F6.boolean.opBoolean","INTERSECT",EDGE,{"disambiguationData":[OD(0.0)],"derivedFrom":[makeQuery(id+"F2.opExtrude","SWEPT_FACE",FACE,{"disambiguationData":[OSD([sQuery(id+"F1.wireOp",EDGE,"E11")])]}),makeQuery(id+"F6.opExtrude","SWEPT_FACE",FACE,{"disambiguationData":[OSD([sQuery(id+"F5.wireOp",EDGE,"E25")])]})]});
            fillet(context, id + "F8", {"entities" : qUnion([Q0, Q1, Q2, Q3, Q4, Q5, Q6, Q7, Q8, Q9, Q10, Q11]), "radius" : 5 * mm, "tangentPropagation" : true, "allowEdgeOverflow" : false});
        }
        {
            var Q0;
            {var subQ0=sQuery(id+"F5.wireOp",EDGE,"E31");var subQ1=sQuery(id+"F5.wireOp",EDGE,"E13");var subQ2=makeQuery(id+"F5.imprint","INTERSECT",VERTEX,{"disambiguationData":[OD(0.0)],"derivedFrom":[subQ1,subQ0]});Q0=makeQuery(id+"F5.imprint","IMPRINT",FACE,{"disambiguationData":[TD([[makeQuery(id+"F5.imprint","IMPRINT",EDGE,{"disambiguationData":[TD([[subQ2,-1.0]])],"derivedFrom":subQ1}),-1.0]])]});}
            var Q1;
            {var subQ0=sQuery(id+"F5.wireOp",EDGE,"E31");var subQ1=sQuery(id+"F5.wireOp",EDGE,"E13");var subQ2=makeQuery(id+"F5.imprint","INTERSECT",VERTEX,{"disambiguationData":[OD(0.0)],"derivedFrom":[subQ1,subQ0]});Q1=makeQuery(id+"F5.imprint","IMPRINT",FACE,{"disambiguationData":[TD([[makeQuery(id+"F5.imprint","IMPRINT",EDGE,{"disambiguationData":[TD([[subQ2,-1.0]])],"derivedFrom":subQ1}),1.0]])]});}
            var Q2;
            {var subQ0=sQuery(id+"F5.wireOp",EDGE,"E32");var subQ1=sQuery(id+"F5.wireOp",EDGE,"E13");var subQ2=makeQuery(id+"F5.imprint","INTERSECT",VERTEX,{"disambiguationData":[OD(0.0)],"derivedFrom":[subQ1,subQ0]});Q2=makeQuery(id+"F5.imprint","IMPRINT",FACE,{"disambiguationData":[TD([[makeQuery(id+"F5.imprint","IMPRINT",EDGE,{"disambiguationData":[TD([[subQ2,-1.0]])],"derivedFrom":subQ1}),-1.0]])]});}
            var Q3;
            {var subQ0=sQuery(id+"F5.wireOp",EDGE,"E32");var subQ1=sQuery(id+"F5.wireOp",EDGE,"E13");var subQ2=makeQuery(id+"F5.imprint","INTERSECT",VERTEX,{"disambiguationData":[OD(0.0)],"derivedFrom":[subQ1,subQ0]});Q3=makeQuery(id+"F5.imprint","IMPRINT",FACE,{"disambiguationData":[TD([[makeQuery(id+"F5.imprint","IMPRINT",EDGE,{"disambiguationData":[TD([[subQ2,-1.0]])],"derivedFrom":subQ1}),1.0]])]});}
            var Q4;
            {var subQ0=sQuery(id+"F5.wireOp",EDGE,"E33");var subQ1=sQuery(id+"F5.wireOp",EDGE,"E13");var subQ2=makeQuery(id+"F5.imprint","INTERSECT",VERTEX,{"disambiguationData":[OD(0.0)],"derivedFrom":[subQ1,subQ0]});Q4=makeQuery(id+"F5.imprint","IMPRINT",FACE,{"disambiguationData":[TD([[makeQuery(id+"F5.imprint","IMPRINT",EDGE,{"disambiguationData":[TD([[subQ2,-1.0]])],"derivedFrom":subQ1}),1.0]])]});}
            var Q5;
            {var subQ0=sQuery(id+"F5.wireOp",EDGE,"E33");var subQ1=sQuery(id+"F5.wireOp",EDGE,"E13");var subQ2=makeQuery(id+"F5.imprint","INTERSECT",VERTEX,{"disambiguationData":[OD(0.0)],"derivedFrom":[subQ1,subQ0]});Q5=makeQuery(id+"F5.imprint","IMPRINT",FACE,{"disambiguationData":[TD([[makeQuery(id+"F5.imprint","IMPRINT",EDGE,{"disambiguationData":[TD([[subQ2,-1.0]])],"derivedFrom":subQ1}),-1.0]])]});}
            var Q6;
            {var subQ0=sQuery(id+"F5.wireOp",EDGE,"E34");var subQ1=sQuery(id+"F5.wireOp",EDGE,"E13");var subQ2=makeQuery(id+"F5.imprint","INTERSECT",VERTEX,{"disambiguationData":[OD(0.0)],"derivedFrom":[subQ1,subQ0]});Q6=makeQuery(id+"F5.imprint","IMPRINT",FACE,{"disambiguationData":[TD([[makeQuery(id+"F5.imprint","IMPRINT",EDGE,{"disambiguationData":[TD([[subQ2,-1.0]])],"derivedFrom":subQ1}),1.0]])]});}
            var Q7;
            {var subQ0=sQuery(id+"F5.wireOp",EDGE,"E34");var subQ1=sQuery(id+"F5.wireOp",EDGE,"E13");var subQ2=makeQuery(id+"F5.imprint","INTERSECT",VERTEX,{"disambiguationData":[OD(0.0)],"derivedFrom":[subQ1,subQ0]});Q7=makeQuery(id+"F5.imprint","IMPRINT",FACE,{"disambiguationData":[TD([[makeQuery(id+"F5.imprint","IMPRINT",EDGE,{"disambiguationData":[TD([[subQ2,-1.0]])],"derivedFrom":subQ1}),-1.0]])]});}
            var Q8;
            {var subQ1=sQuery(id+"F5.wireOp",EDGE,"E36.bottom");Q8=makeQuery(id+"F5.imprint","IMPRINT",FACE,{"disambiguationData":[TD([[makeQuery(id+"F5.imprint","IMPRINT",EDGE,{"derivedFrom":subQ1}),-1.0]])]});}
            var Q9;
            {var subQ0=sQuery(id+"F5.wireOp",EDGE,"E36.top");var subQ1=sQuery(id+"F5.wireOp",EDGE,"E13");var subQ2=makeQuery(id+"F5.imprint","INTERSECT",VERTEX,{"derivedFrom":[subQ1,subQ0]});Q9=makeQuery(id+"F5.imprint","IMPRINT",FACE,{"disambiguationData":[TD([[makeQuery(id+"F5.imprint","IMPRINT",EDGE,{"disambiguationData":[TD([[subQ2,-1.0]])],"derivedFrom":subQ1}),1.0]])]});}
            var Q10;
            {var subQ0=sQuery(id+"F5.wireOp",EDGE,"E35");var subQ1=sQuery(id+"F5.wireOp",EDGE,"E13");var subQ2=makeQuery(id+"F5.imprint","INTERSECT",VERTEX,{"disambiguationData":[OD(0.0)],"derivedFrom":[subQ1,subQ0]});Q10=makeQuery(id+"F5.imprint","IMPRINT",FACE,{"disambiguationData":[TD([[makeQuery(id+"F5.imprint","IMPRINT",EDGE,{"disambiguationData":[TD([[subQ2,-1.0]])],"derivedFrom":subQ1}),-1.0]])]});}
            var Q11;
            {var subQ0=sQuery(id+"F5.wireOp",EDGE,"E35");var subQ1=sQuery(id+"F5.wireOp",EDGE,"E13");var subQ2=makeQuery(id+"F5.imprint","INTERSECT",VERTEX,{"disambiguationData":[OD(0.0)],"derivedFrom":[subQ1,subQ0]});Q11=makeQuery(id+"F5.imprint","IMPRINT",FACE,{"disambiguationData":[TD([[makeQuery(id+"F5.imprint","IMPRINT",EDGE,{"disambiguationData":[TD([[subQ2,-1.0]])],"derivedFrom":subQ1}),1.0]])]});}
            extrude(context, id + "F9", {"entities" : qUnion([Q0, Q1, Q2, Q3, Q4, Q5, Q6, Q7, Q8, Q9, Q10, Q11]), "operationType" : NewBodyOperationType.ADD, "depth" : 8 * mm, "offsetDistance" : 25 * mm});
        }
        {
            var Q0;
            Q0=makeQuery(id+"F9.opExtrude","CAP_EDGE",EDGE,{"disambiguationData":[OSD([sQuery(id+"F5.wireOp",EDGE,"E35")])],"isStart":false});
            var Q1;
            Q1=makeQuery(id+"F9.opExtrude","CAP_FACE",FACE,{"disambiguationData":[OSD([sQuery(id+"F5.wireOp",EDGE,"E31")])],"isStart":false});
            var Q2;
            Q2=makeQuery(id+"F9.opExtrude","CAP_FACE",FACE,{"disambiguationData":[OSD([sQuery(id+"F5.wireOp",EDGE,"E32")])],"isStart":false});
            var Q3;
            Q3=makeQuery(id+"F9.opExtrude","CAP_FACE",FACE,{"disambiguationData":[OSD([sQuery(id+"F5.wireOp",EDGE,"E33")])],"isStart":false});
            var Q4;
            Q4=makeQuery(id+"F9.opExtrude","CAP_FACE",FACE,{"disambiguationData":[OSD([sQuery(id+"F5.wireOp",EDGE,"E34")])],"isStart":false});
            var Q5;
            Q5=makeQuery(id+"F9.opExtrude","CAP_EDGE",EDGE,{"disambiguationData":[OSD([sQuery(id+"F5.wireOp",EDGE,"E36.left")])],"isStart":false});
            var Q6;
            Q6=makeQuery(id+"F9.opExtrude","CAP_EDGE",EDGE,{"disambiguationData":[OSD([sQuery(id+"F5.wireOp",EDGE,"E36.right")])],"isStart":false});
            var Q7;
            Q7=makeQuery(id+"F9.opExtrude","CAP_EDGE",EDGE,{"disambiguationData":[OSD([sQuery(id+"F5.wireOp",EDGE,"E36.bottom")])],"isStart":false});
            var Q8;
            Q8=makeQuery(id+"F9.opExtrude","CAP_EDGE",EDGE,{"disambiguationData":[OSD([sQuery(id+"F5.wireOp",EDGE,"E36.top")])],"isStart":false});
            fillet(context, id + "F10", {"entities" : qUnion([Q0, Q1, Q2, Q3, Q4, Q5, Q6, Q7, Q8]), "radius" : .45 * mm, "tangentPropagation" : true, "allowEdgeOverflow" : false});
        }
        {
            var Q0;
            {var subQ0=sQuery(id+"F5.wireOp",EDGE,"E35");var subQ1=sQuery(id+"F5.wireOp",EDGE,"E13");var subQ2=makeQuery(id+"F5.imprint","INTERSECT",VERTEX,{"disambiguationData":[OD(0.0)],"derivedFrom":[subQ1,subQ0]});Q0=makeQuery(id+"F5.imprint","IMPRINT",FACE,{"disambiguationData":[TD([[makeQuery(id+"F5.imprint","IMPRINT",EDGE,{"disambiguationData":[TD([[subQ2,-1.0]])],"derivedFrom":subQ1}),-1.0]])]});}
            var Q1;
            {var subQ0=sQuery(id+"F5.wireOp",EDGE,"E35");var subQ1=sQuery(id+"F5.wireOp",EDGE,"E13");var subQ2=makeQuery(id+"F5.imprint","INTERSECT",VERTEX,{"disambiguationData":[OD(0.0)],"derivedFrom":[subQ1,subQ0]});Q1=makeQuery(id+"F5.imprint","IMPRINT",FACE,{"disambiguationData":[TD([[makeQuery(id+"F5.imprint","IMPRINT",EDGE,{"disambiguationData":[TD([[subQ2,-1.0]])],"derivedFrom":subQ1}),1.0]])]});}
            var Q2;
            {var subQ1=sQuery(id+"F5.wireOp",EDGE,"E36.bottom");Q2=makeQuery(id+"F5.imprint","IMPRINT",FACE,{"disambiguationData":[TD([[makeQuery(id+"F5.imprint","IMPRINT",EDGE,{"derivedFrom":subQ1}),-1.0]])]});}
            var Q3;
            {var subQ0=sQuery(id+"F5.wireOp",EDGE,"E36.top");var subQ1=sQuery(id+"F5.wireOp",EDGE,"E13");var subQ2=makeQuery(id+"F5.imprint","INTERSECT",VERTEX,{"derivedFrom":[subQ1,subQ0]});Q3=makeQuery(id+"F5.imprint","IMPRINT",FACE,{"disambiguationData":[TD([[makeQuery(id+"F5.imprint","IMPRINT",EDGE,{"disambiguationData":[TD([[subQ2,-1.0]])],"derivedFrom":subQ1}),1.0]])]});}
            var Q4;
            {var subQ0=sQuery(id+"F5.wireOp",EDGE,"E34");var subQ1=sQuery(id+"F5.wireOp",EDGE,"E13");var subQ2=makeQuery(id+"F5.imprint","INTERSECT",VERTEX,{"disambiguationData":[OD(0.0)],"derivedFrom":[subQ1,subQ0]});Q4=makeQuery(id+"F5.imprint","IMPRINT",FACE,{"disambiguationData":[TD([[makeQuery(id+"F5.imprint","IMPRINT",EDGE,{"disambiguationData":[TD([[subQ2,-1.0]])],"derivedFrom":subQ1}),1.0]])]});}
            var Q5;
            {var subQ0=sQuery(id+"F5.wireOp",EDGE,"E34");var subQ1=sQuery(id+"F5.wireOp",EDGE,"E13");var subQ2=makeQuery(id+"F5.imprint","INTERSECT",VERTEX,{"disambiguationData":[OD(0.0)],"derivedFrom":[subQ1,subQ0]});Q5=makeQuery(id+"F5.imprint","IMPRINT",FACE,{"disambiguationData":[TD([[makeQuery(id+"F5.imprint","IMPRINT",EDGE,{"disambiguationData":[TD([[subQ2,-1.0]])],"derivedFrom":subQ1}),-1.0]])]});}
            var Q6;
            {var subQ0=sQuery(id+"F5.wireOp",EDGE,"E33");var subQ1=sQuery(id+"F5.wireOp",EDGE,"E13");var subQ2=makeQuery(id+"F5.imprint","INTERSECT",VERTEX,{"disambiguationData":[OD(0.0)],"derivedFrom":[subQ1,subQ0]});Q6=makeQuery(id+"F5.imprint","IMPRINT",FACE,{"disambiguationData":[TD([[makeQuery(id+"F5.imprint","IMPRINT",EDGE,{"disambiguationData":[TD([[subQ2,-1.0]])],"derivedFrom":subQ1}),1.0]])]});}
            var Q7;
            {var subQ0=sQuery(id+"F5.wireOp",EDGE,"E33");var subQ1=sQuery(id+"F5.wireOp",EDGE,"E13");var subQ2=makeQuery(id+"F5.imprint","INTERSECT",VERTEX,{"disambiguationData":[OD(0.0)],"derivedFrom":[subQ1,subQ0]});Q7=makeQuery(id+"F5.imprint","IMPRINT",FACE,{"disambiguationData":[TD([[makeQuery(id+"F5.imprint","IMPRINT",EDGE,{"disambiguationData":[TD([[subQ2,-1.0]])],"derivedFrom":subQ1}),-1.0]])]});}
            var Q8;
            {var subQ0=sQuery(id+"F5.wireOp",EDGE,"E32");var subQ1=sQuery(id+"F5.wireOp",EDGE,"E13");var subQ2=makeQuery(id+"F5.imprint","INTERSECT",VERTEX,{"disambiguationData":[OD(0.0)],"derivedFrom":[subQ1,subQ0]});Q8=makeQuery(id+"F5.imprint","IMPRINT",FACE,{"disambiguationData":[TD([[makeQuery(id+"F5.imprint","IMPRINT",EDGE,{"disambiguationData":[TD([[subQ2,-1.0]])],"derivedFrom":subQ1}),1.0]])]});}
            var Q9;
            {var subQ0=sQuery(id+"F5.wireOp",EDGE,"E32");var subQ1=sQuery(id+"F5.wireOp",EDGE,"E13");var subQ2=makeQuery(id+"F5.imprint","INTERSECT",VERTEX,{"disambiguationData":[OD(0.0)],"derivedFrom":[subQ1,subQ0]});Q9=makeQuery(id+"F5.imprint","IMPRINT",FACE,{"disambiguationData":[TD([[makeQuery(id+"F5.imprint","IMPRINT",EDGE,{"disambiguationData":[TD([[subQ2,-1.0]])],"derivedFrom":subQ1}),-1.0]])]});}
            var Q10;
            {var subQ0=sQuery(id+"F5.wireOp",EDGE,"E31");var subQ1=sQuery(id+"F5.wireOp",EDGE,"E13");var subQ2=makeQuery(id+"F5.imprint","INTERSECT",VERTEX,{"disambiguationData":[OD(0.0)],"derivedFrom":[subQ1,subQ0]});Q10=makeQuery(id+"F5.imprint","IMPRINT",FACE,{"disambiguationData":[TD([[makeQuery(id+"F5.imprint","IMPRINT",EDGE,{"disambiguationData":[TD([[subQ2,-1.0]])],"derivedFrom":subQ1}),-1.0]])]});}
            var Q11;
            {var subQ0=sQuery(id+"F5.wireOp",EDGE,"E31");var subQ1=sQuery(id+"F5.wireOp",EDGE,"E13");var subQ2=makeQuery(id+"F5.imprint","INTERSECT",VERTEX,{"disambiguationData":[OD(0.0)],"derivedFrom":[subQ1,subQ0]});Q11=makeQuery(id+"F5.imprint","IMPRINT",FACE,{"disambiguationData":[TD([[makeQuery(id+"F5.imprint","IMPRINT",EDGE,{"disambiguationData":[TD([[subQ2,-1.0]])],"derivedFrom":subQ1}),1.0]])]});}
            extrude(context, id + "F11", {"entities" : qUnion([Q0, Q1, Q2, Q3, Q4, Q5, Q6, Q7, Q8, Q9, Q10, Q11]), "operationType" : NewBodyOperationType.REMOVE, "depth" : 1.8 * mm, "offsetDistance" : 25 * mm});
        }
        {
            var Q0;
            Q0=qCreatedBy(makeId("Top.planeOp"),FACE);
            var sketch = newSketch(context, id + "F12", { "sketchPlane" : qUnion([Q0])});
            skCircle(sketch, "E37", {"center": v(0, 0) * mm, "radius": 13.47 * mm});
            skSolve(sketch);
        }
        {
            var Q0;
            Q0=makeQuery(id+"F12.imprint","IMPRINT",FACE,{"disambiguationData":[TD([[makeQuery(id+"F12.imprint","IMPRINT",EDGE,{"derivedFrom":sQuery(id+"F12.wireOp",EDGE,"E37")}),1.0]])]});
            extrude(context, id + "F13", {"entities" : qUnion([Q0]), "operationType" : NewBodyOperationType.REMOVE, "depth" : 1 * mm, "offsetDistance" : 25 * mm});
        }
        {
            var Q0;
            {var subQ0=sQuery(id+"F0.wireOp",EDGE,"E3.right");var subQ1=sQuery(id+"F0.wireOp",EDGE,"E1.0");var subQ2=makeQuery(id+"F0.imprint","INTERSECT",VERTEX,{"disambiguationData":[OD(0.0)],"derivedFrom":[subQ1,subQ0]});Q0=makeQuery(id+"F0.imprint","IMPRINT",FACE,{"disambiguationData":[TD([[makeQuery(id+"F0.imprint","IMPRINT",EDGE,{"disambiguationData":[TD([[subQ2,1.0]])],"derivedFrom":subQ1}),1.0]])]});}
            var Q1;
            {var subQ0=sQuery(id+"F0.wireOp",EDGE,"E9.left");var subQ1=sQuery(id+"F0.wireOp",EDGE,"E1.0");var subQ2=makeQuery(id+"F0.imprint","INTERSECT",VERTEX,{"disambiguationData":[OD(0.0)],"derivedFrom":[subQ1,subQ0]});Q1=makeQuery(id+"F0.imprint","IMPRINT",FACE,{"disambiguationData":[TD([[makeQuery(id+"F0.imprint","IMPRINT",EDGE,{"disambiguationData":[TD([[subQ2,-1.0]])],"derivedFrom":subQ1}),1.0]])]});}
            var Q2;
            {var subQ0=sQuery(id+"F0.wireOp",EDGE,"E7.top");var subQ1=sQuery(id+"F0.wireOp",EDGE,"E1.0");var subQ2=makeQuery(id+"F0.imprint","INTERSECT",VERTEX,{"disambiguationData":[OD(0.0)],"derivedFrom":[subQ1,subQ0]});Q2=makeQuery(id+"F0.imprint","IMPRINT",FACE,{"disambiguationData":[TD([[makeQuery(id+"F0.imprint","IMPRINT",EDGE,{"disambiguationData":[TD([[subQ2,-1.0]])],"derivedFrom":subQ1}),1.0]])]});}
            extrude(context, id + "F14", {"entities" : qUnion([Q0, Q1, Q2]), "operationType" : NewBodyOperationType.REMOVE, "depth" : 1 * mm, "offsetDistance" : 25 * mm});
        }
        {
            var Q0;
            Q0=makeQuery(id+"F14.boolean.opBoolean","COPY",EDGE,{"derivedFrom":makeQuery(id+"F14.opExtrude","SWEPT_EDGE",EDGE,{"disambiguationData":[OSD([sQuery(id+"F0.wireOp",EDGE,"E1.0"),sQuery(id+"F0.wireOp",EDGE,"E9.left")])]})});
            var Q1;
            Q1=makeQuery(id+"F14.boolean.opBoolean","COPY",EDGE,{"derivedFrom":makeQuery(id+"F14.opExtrude","SWEPT_EDGE",EDGE,{"disambiguationData":[OSD([sQuery(id+"F0.wireOp",EDGE,"E1.0"),sQuery(id+"F0.wireOp",EDGE,"E3.right")])]})});
            var Q2;
            Q2=makeQuery(id+"F14.boolean.opBoolean","COPY",EDGE,{"derivedFrom":makeQuery(id+"F14.opExtrude","SWEPT_EDGE",EDGE,{"disambiguationData":[OSD([sQuery(id+"F0.wireOp",EDGE,"E1.0"),sQuery(id+"F0.wireOp",EDGE,"E7.top")])]})});
            var Q3;
            {var subQ0=sQuery(id+"F0.wireOp",EDGE,"E6.bottom");var subQ1=sQuery(id+"F0.wireOp",EDGE,"E1.0");Q3=makeQuery(id+"F14.boolean.opBoolean","COPY",EDGE,{"derivedFrom":makeQuery(id+"F14.opExtrude","SWEPT_EDGE",EDGE,{"disambiguationData":[OSD([subQ1,subQ0]),TDD([makeQuery(id+"F0.imprint","INTERSECT",VERTEX,{"disambiguationData":[OD(1.0)],"derivedFrom":[subQ1,subQ0]})])]})});}
            var Q4;
            {var subQ0=sQuery(id+"F0.wireOp",EDGE,"E6.bottom");var subQ1=sQuery(id+"F0.wireOp",EDGE,"E1.0");Q4=makeQuery(id+"F14.boolean.opBoolean","COPY",EDGE,{"derivedFrom":makeQuery(id+"F14.opExtrude","SWEPT_EDGE",EDGE,{"disambiguationData":[OSD([subQ1,subQ0]),TDD([makeQuery(id+"F0.imprint","INTERSECT",VERTEX,{"disambiguationData":[OD(0.0)],"derivedFrom":[subQ1,subQ0]})])]})});}
            var Q5;
            Q5=makeQuery(id+"F14.boolean.opBoolean","COPY",EDGE,{"derivedFrom":makeQuery(id+"F14.opExtrude","SWEPT_EDGE",EDGE,{"disambiguationData":[OSD([sQuery(id+"F0.wireOp",EDGE,"E1.0"),sQuery(id+"F0.wireOp",EDGE,"E7.bottom")])]})});
            fillet(context, id + "F15", {"entities" : qUnion([Q0, Q1, Q2, Q3, Q4, Q5]), "radius" : 1 * mm, "tangentPropagation" : true, "allowEdgeOverflow" : false});
        }
    });
